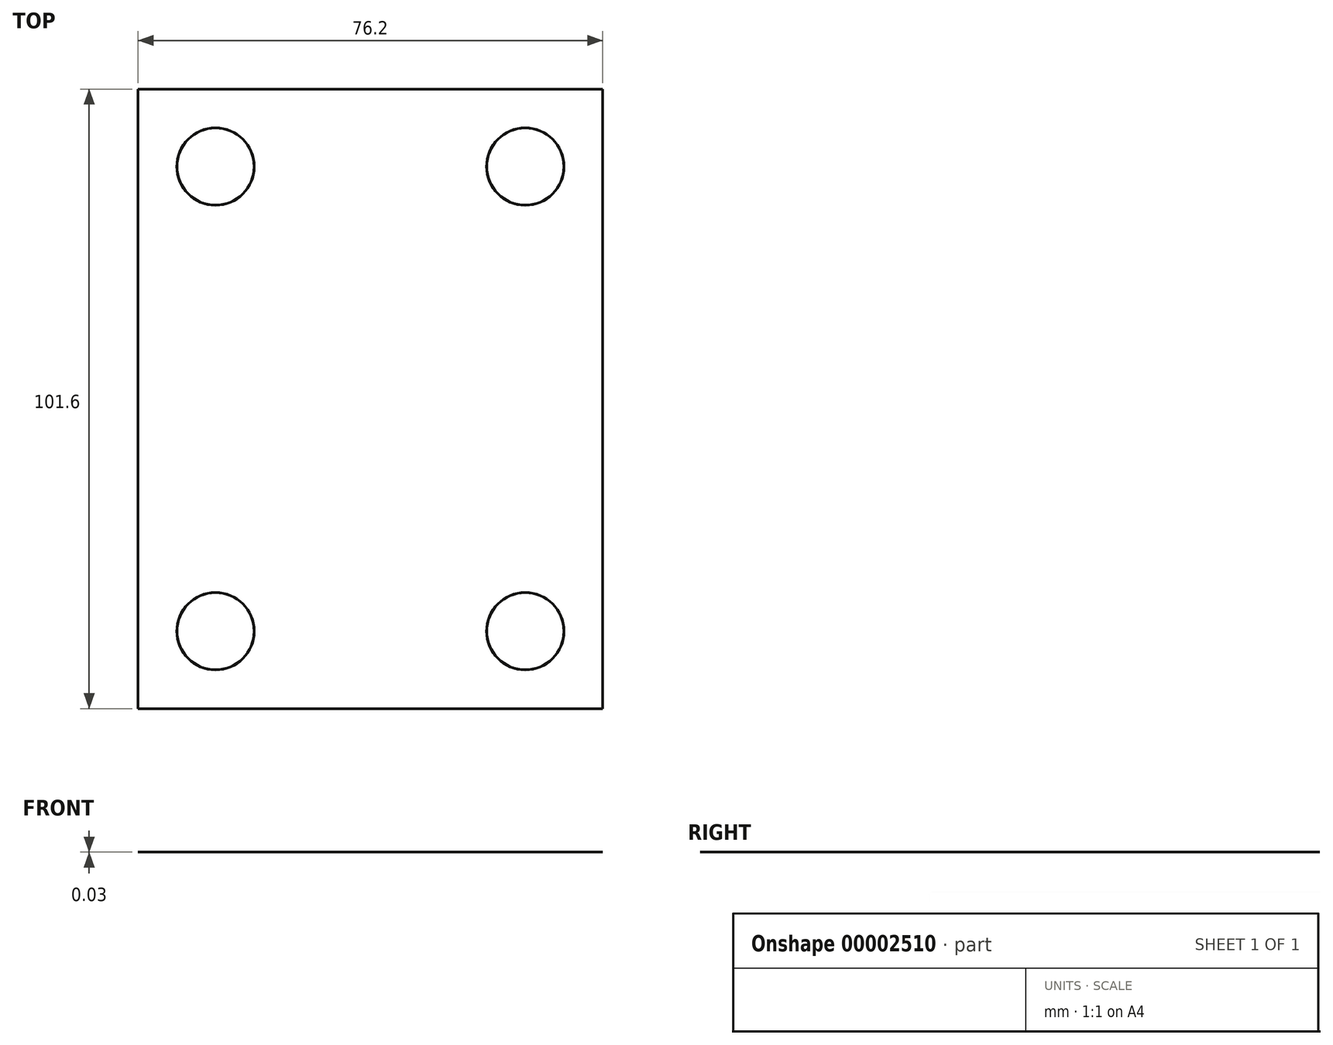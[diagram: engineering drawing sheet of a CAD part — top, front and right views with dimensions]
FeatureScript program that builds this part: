
annotation { "Feature Type Name" : "Feature", "Feature Type Description" : "" }
export const myFeature = defineFeature(function(context is Context, id is Id, definition is map)
    precondition{}
    {
        {
            var Q0;
            Q0=qCreatedBy(makeId("Top.planeOp"),FACE);
            var sketch = newSketch(context, id + "F0", { "sketchPlane" : qUnion([Q0])});
            skLineSegment(sketch, "E0.bottom", {"start": v(0, 0) * mm, "end": v(76.2, 0) * mm});
            skLineSegment(sketch, "E0.top", {"start": v(0, 101.6) * mm, "end": v(76.2, 101.6) * mm});
            skLineSegment(sketch, "E0.left", {"start": v(0, 0) * mm, "end": v(0, 101.6) * mm});
            skLineSegment(sketch, "E0.right", {"start": v(76.2, 0) * mm, "end": v(76.2, 101.6) * mm});
            skSolve(sketch);
        }
        {
            var Q0;
            Q0=makeQuery(id+"F0.imprint","IMPRINT",FACE,{"disambiguationData":[TD([[makeQuery(id+"F0.imprint","IMPRINT",EDGE,{"derivedFrom":sQuery(id+"F0.wireOp",EDGE,"E0.bottom")}),1.0]])]});
            extrude(context, id + "F1", {"entities" : qUnion([Q0]), "depth" : 3 / 101.6 * mm});
        }
        {
            var Q0;
            Q0=makeQuery(id+"F1.opExtrude","CAP_FACE",FACE,{"disambiguationData":[OSD([sQuery(id+"F0.wireOp",EDGE,"E0.bottom"),sQuery(id+"F0.wireOp",EDGE,"E0.top"),sQuery(id+"F0.wireOp",EDGE,"E0.left"),sQuery(id+"F0.wireOp",EDGE,"E0.right")])],"isStart":false});
            var sketch = newSketch(context, id + "F2", { "sketchPlane" : qUnion([Q0])});
            skLineSegment(sketch, "E1.0", {"start": v(12.7, 88.9) * mm, "end": v(63.5, 88.9) * mm});
            skLineSegment(sketch, "E1.1", {"start": v(12.7, 12.7) * mm, "end": v(12.7, 88.9) * mm});
            skLineSegment(sketch, "E1.2", {"start": v(12.7, 12.7) * mm, "end": v(63.5, 12.7) * mm});
            skLineSegment(sketch, "E1.3", {"start": v(63.5, 12.7) * mm, "end": v(63.5, 88.9) * mm});
            skLineSegment(sketch, "E2.0", {"start": v(6.35, 95.25) * mm, "end": v(6.35, 6.35) * mm});
            skLineSegment(sketch, "E2.1", {"start": v(69.85, 95.25) * mm, "end": v(6.35, 95.25) * mm});
            skLineSegment(sketch, "E2.2", {"start": v(69.85, 6.35) * mm, "end": v(69.85, 95.25) * mm});
            skLineSegment(sketch, "E2.3", {"start": v(6.35, 6.35) * mm, "end": v(69.85, 6.35) * mm});
            skSolve(sketch);
        }
        {
            var Q0;
            Q0=sQuery(id+"F2.wireOp",VERTEX,"E1.0.end");
            var Q1;
            Q1=sQuery(id+"F2.wireOp",VERTEX,"E1.3.start");
            var Q2;
            Q2=sQuery(id+"F2.wireOp",VERTEX,"E1.2.start");
            var Q3;
            Q3=sQuery(id+"F2.wireOp",VERTEX,"E1.1.end");
            var Q4;
            Q4=makeQuery(id+"F1.opExtrude","SWEPT_BODY",BODY,{"disambiguationData":[OSD([sQuery(id+"F0.wireOp",EDGE,"E0.bottom"),sQuery(id+"F0.wireOp",EDGE,"E0.top"),sQuery(id+"F0.wireOp",EDGE,"E0.left"),sQuery(id+"F0.wireOp",EDGE,"E0.right")])]});
            hole(context, id + "F3", {"style" : HoleStyle.C_SINK, "holeDiameter" : 6.35 * mm, "cSinkDiameter" : 12.7 * mm, "endStyle" : HoleEndStyle.THROUGH, "locations" : qUnion([Q0, Q1, Q2, Q3]), "scope" : qUnion([Q4]), "cSinkAngle" : 90 * degree});
        }
    });
